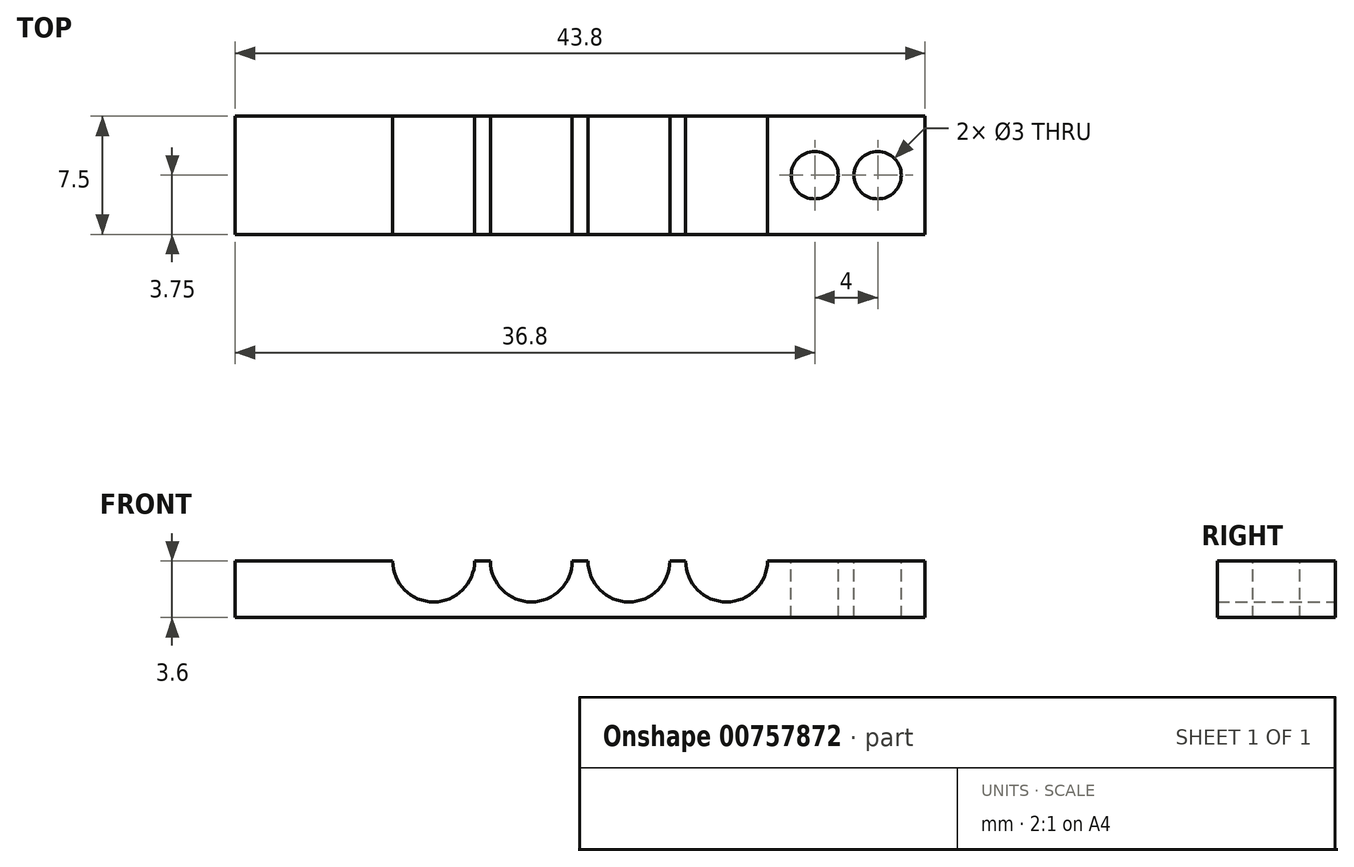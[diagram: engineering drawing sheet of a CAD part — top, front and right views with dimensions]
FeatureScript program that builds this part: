
annotation { "Feature Type Name" : "Feature", "Feature Type Description" : "" }
export const myFeature = defineFeature(function(context is Context, id is Id, definition is map)
    precondition{}
    {
        {
            var Q0;
            Q0=qCreatedBy(makeId("Front.planeOp"),FACE);
            var sketch = newSketch(context, id + "F0", { "sketchPlane" : qUnion([Q0])});
            skLineSegment(sketch, "E0.bottom", {"start": v(-21.9, 3.6) * mm, "end": v(21.9, 3.6) * mm});
            skLineSegment(sketch, "E0.top", {"start": v(-21.9, 0) * mm, "end": v(21.9, 0) * mm});
            skLineSegment(sketch, "E0.left", {"start": v(-21.9, 3.6) * mm, "end": v(-21.9, 0) * mm});
            skLineSegment(sketch, "E0.right", {"start": v(21.9, 3.6) * mm, "end": v(21.9, 0) * mm});
            skCircle(sketch, "E1", {"center": v(-9.3, 3.6) * mm, "radius": 2.6 * mm});
            skCircle(sketch, "E2", {"center": v(-3.1, 3.6) * mm, "radius": 2.6 * mm});
            skCircle(sketch, "E3", {"center": v(3.1, 3.6) * mm, "radius": 2.6 * mm});
            skCircle(sketch, "E4", {"center": v(9.3, 3.6) * mm, "radius": 2.6 * mm});
            skSolve(sketch);
        }
        {
            var Q0;
            Q0=makeQuery(id+"F0.imprint","IMPRINT",FACE,{"disambiguationData":[TD([[makeQuery(id+"F0.imprint","IMPRINT",EDGE,{"derivedFrom":sQuery(id+"F0.wireOp",EDGE,"E0.top")}),1.0]])]});
            extrude(context, id + "F1", {"entities" : qUnion([Q0]), "depth" : 7.5 * mm, "offsetDistance" : 25 * mm});
        }
        {
            var Q0;
            {var subQ0=sQuery(id+"F0.wireOp",EDGE,"E0.bottom");Q0=makeQuery(id+"F1.opExtrude","SWEPT_FACE",FACE,{"disambiguationData":[OSD([subQ0]),TDD([makeQuery(id+"F0.imprint","IMPRINT",EDGE,{"disambiguationData":[TD([[makeQuery(id+"F0.imprint","INTERSECT",VERTEX,{"derivedFrom":[subQ0,sQuery(id+"F0.wireOp",EDGE,"E0.right")]}),1.0]])],"derivedFrom":subQ0})])]});}
            var sketch = newSketch(context, id + "F2", { "sketchPlane" : qUnion([Q0])});
            skLineSegment(sketch, "E5", {"start": v(21.9, -3.75) * mm, "end": v(-21.93, -3.75) * mm, "construction": true});
            skLineSegment(sketch, "E6", {"start": v(18.9, -7.5) * mm, "end": v(18.9, 0) * mm, "construction": true});
            skLineSegment(sketch, "E7", {"start": v(14.9, -7.5) * mm, "end": v(14.9, 0) * mm, "construction": true});
            skCircle(sketch, "E8", {"center": v(18.9, -3.75) * mm, "radius": 1.5 * mm});
            skCircle(sketch, "E9", {"center": v(14.9, -3.75) * mm, "radius": 1.5 * mm});
            skSolve(sketch);
        }
        {
            var Q0;
            Q0 = qSketchRegion(id + "F2", true);
            extrude(context, id + "F3", {"entities" : qUnion([Q0]), "operationType" : NewBodyOperationType.REMOVE, "oppositeDirection" : true, "depth" : 25 * mm, "offsetDistance" : 25 * mm});
        }
    });
